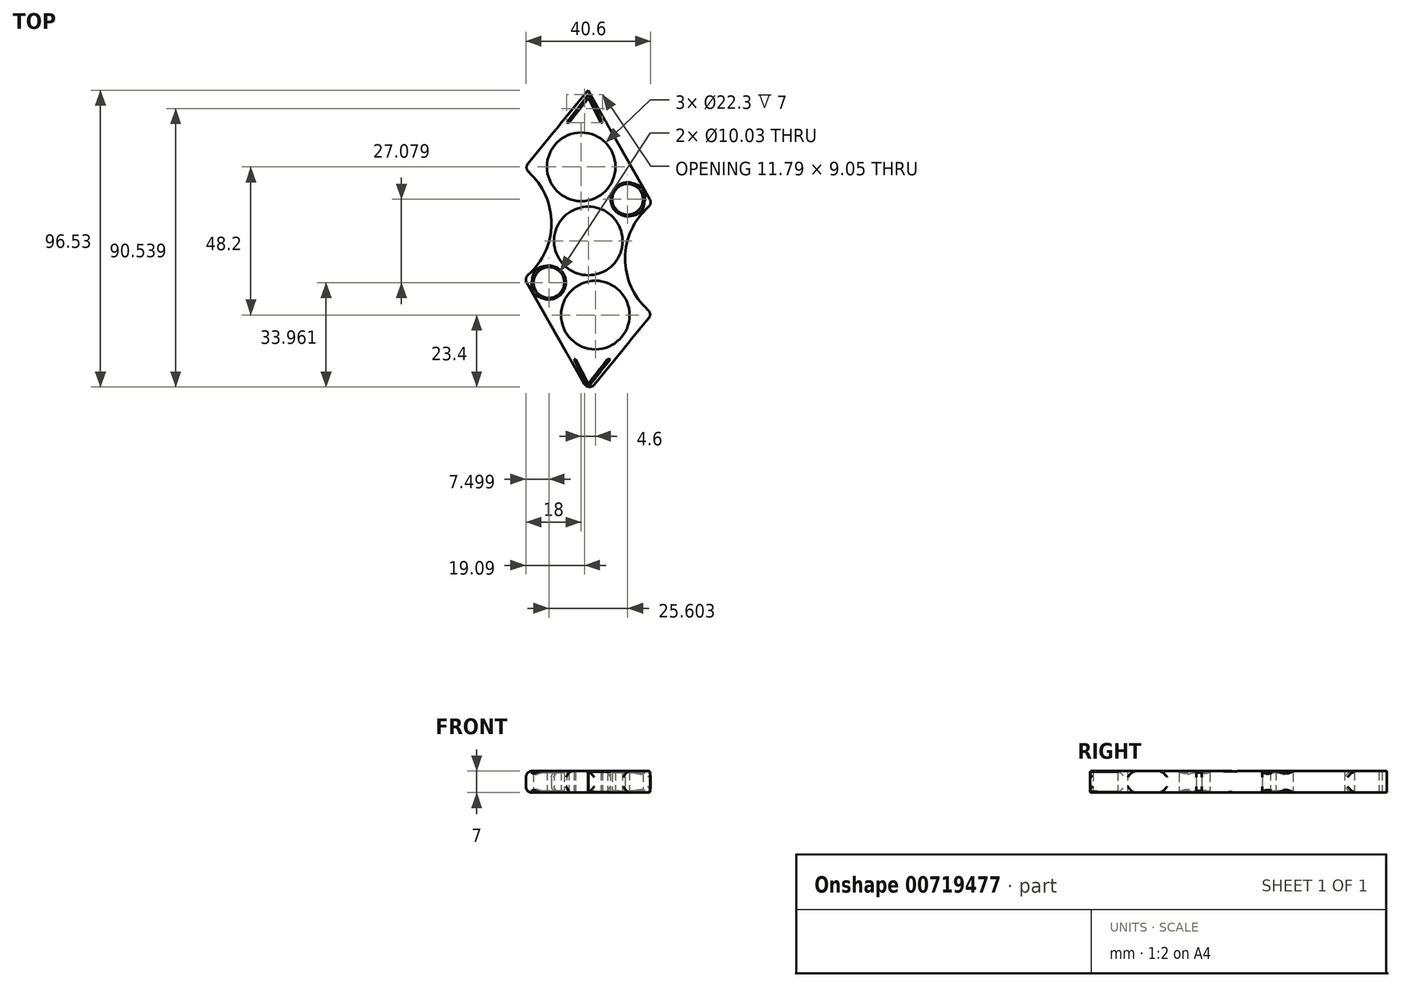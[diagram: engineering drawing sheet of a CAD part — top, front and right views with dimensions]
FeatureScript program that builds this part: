
annotation { "Feature Type Name" : "Feature", "Feature Type Description" : "" }
export const myFeature = defineFeature(function(context is Context, id is Id, definition is map)
    precondition{}
    {
        {
            var Q0;
            Q0=qCreatedBy(makeId("Top.planeOp"),FACE);
            var sketch = newSketch(context, id + "F0", { "sketchPlane" : qUnion([Q0])});
            skCircle(sketch, "E0", {"center": v(0, 0) * mm, "radius": 11.15 * mm});
            skCircle(sketch, "E1", {"center": v(0, 0) * mm, "radius": 12.15 * mm});
            skPoint(sketch, "E2", {"position": v(0, 12.15) * mm});
            skPoint(sketch, "E3", {"position": v(0, -12.15) * mm});
            skPoint(sketch, "E4", {"position": v(-20.9, 23.65) * mm});
            skLineSegment(sketch, "E5", {"start": v(-20.9, 23.65) * mm, "end": v(-9.47, 37.54) * mm});
            skCircle(sketch, "E6.1.0.0", {"center": v(-2.3, 24.1) * mm, "radius": 11.15 * mm});
            skCircle(sketch, "E6.1.0.1", {"center": v(-2.3, 24.1) * mm, "radius": 12.15 * mm});
            skLineSegment(sketch, "E6.direction1", {"start": v(0, 0) * mm, "end": v(-2.3, 24.1) * mm, "construction": true});
            skPoint(sketch, "E7.orphan", {"position": v(-11.2, 12.15) * mm});
            skLineSegment(sketch, "E8.1.0", {"start": v(20.9, -23.65) * mm, "end": v(11.35, -35.25) * mm});
            skLineSegment(sketch, "E8.1.1", {"start": v(-7.16, -36.23) * mm, "end": v(-20.88, -12.14) * mm});
            skPoint(sketch, "E9.orphan", {"position": v(10.73, -12.15) * mm});
            skCircle(sketch, "E10.1.0", {"center": v(2.3, -24.1) * mm, "radius": 11.15 * mm});
            skCircle(sketch, "E10.1.1", {"center": v(2.3, -24.1) * mm, "radius": 12.15 * mm});
            skCircle(sketch, "E11", {"center": v(12.8, 13.54) * mm, "radius": 5.01 * mm});
            skCircle(sketch, "E12.1.0", {"center": v(-12.8, -13.54) * mm, "radius": 5.01 * mm});
            skPoint(sketch, "E13.orphan", {"position": v(0, 60.23) * mm});
            skPoint(sketch, "E14.orphan", {"position": v(-16.16, 31.2) * mm});
            skPoint(sketch, "E15.orphan", {"position": v(0, 56.97) * mm});
            skPoint(sketch, "E16.orphan", {"position": v(15.33, 24.1) * mm});
            skPoint(sketch, "E17.orphan", {"position": v(0, -60.23) * mm});
            skPoint(sketch, "E18.orphan", {"position": v(-0.02, -56.98) * mm});
            skPoint(sketch, "E19.orphan", {"position": v(16.16, -31.2) * mm});
            skPoint(sketch, "E20.orphan", {"position": v(0, 49.07) * mm});
            skPoint(sketch, "E21.orphan", {"position": v(0, 51.35) * mm});
            skPoint(sketch, "E22.orphan", {"position": v(0, 53.8) * mm});
            skPoint(sketch, "E23.orphan", {"position": v(0.08, -48.94) * mm});
            skLineSegment(sketch, "E24.1.0", {"start": v(-7.16, -36.23) * mm, "end": v(0.08, -49.03) * mm});
            skLineSegment(sketch, "E24.1.3", {"start": v(11.35, -35.25) * mm, "end": v(0.08, -49.03) * mm});
            skPoint(sketch, "E25.orphan", {"position": v(11.27, -37.54) * mm});
            skPoint(sketch, "E26.orphan", {"position": v(10.41, -37.54) * mm});
            skPoint(sketch, "E27.orphan", {"position": v(-11.27, 37.54) * mm});
            skPoint(sketch, "E28.orphan", {"position": v(-10.41, 37.54) * mm});
            skPoint(sketch, "E29.center", {"position": v(0.04, 0.02) * mm});
            skPoint(sketch, "E30.start.orphan", {"position": v(20.88, 12.15) * mm});
            skPoint(sketch, "E31.orphan", {"position": v(20.88, 12.14) * mm});
            skPoint(sketch, "E32.orphan", {"position": v(20.96, 12.7) * mm});
            skPoint(sketch, "E33.orphan", {"position": v(-20.66, -12.66) * mm});
            skPoint(sketch, "E34.start.orphan", {"position": v(-20.88, -12.14) * mm});
            skLineSegment(sketch, "E35", {"start": v(-20.9, -12.15) * mm, "end": v(-20.9, -12.15) * mm});
            skArc(sketch, "E36", {"start": v(-20.88, -12.14) * mm, "mid": v(-11.98, 5.76) * mm, "end": v(-20.9, 23.65) * mm});
            skPoint(sketch, "E37.orphan", {"position": v(-8.87, -37.46) * mm});
            skPoint(sketch, "E38.orphan", {"position": v(-7.98, -37.46) * mm});
            skPoint(sketch, "E39.start.orphan", {"position": v(-20.88, -12.66) * mm});
            skLineSegment(sketch, "E40.1.0", {"start": v(7.16, 36.23) * mm, "end": v(20.88, 12.14) * mm});
            skLineSegment(sketch, "E40.1.1", {"start": v(7.16, 36.23) * mm, "end": v(-0.08, 49.03) * mm});
            skLineSegment(sketch, "E40.1.2", {"start": v(-11.35, 35.25) * mm, "end": v(-0.08, 49.03) * mm});
            skLineSegment(sketch, "E40.1.3", {"start": v(-20.9, 23.65) * mm, "end": v(-11.35, 35.25) * mm});
            skArc(sketch, "E40.1.5", {"start": v(20.88, 12.14) * mm, "mid": v(11.98, -5.76) * mm, "end": v(20.9, -23.65) * mm});
            skPoint(sketch, "E41.middle", {"position": v(-1.24, 37.73) * mm});
            skPoint(sketch, "E42.middle", {"position": v(-1.2, 39.16) * mm});
            skLineSegment(sketch, "E43.bottom", {"start": v(4.69, 38.51) * mm, "end": v(-7.1, 38.51) * mm});
            skLineSegment(sketch, "E43.top", {"start": v(4.69, 37.5) * mm, "end": v(-7.1, 37.5) * mm});
            skLineSegment(sketch, "E43.left", {"start": v(4.69, 38.51) * mm, "end": v(4.69, 37.5) * mm});
            skLineSegment(sketch, "E43.right", {"start": v(-7.1, 38.51) * mm, "end": v(-7.1, 37.5) * mm});
            skPoint(sketch, "E43.middle", {"position": v(-1.2, 38.01) * mm});
            skLineSegment(sketch, "E44", {"start": v(-7.1, 38.51) * mm, "end": v(0, 47.56) * mm});
            skLineSegment(sketch, "E45", {"start": v(0, 47.56) * mm, "end": v(4.69, 38.51) * mm});
            skLineSegment(sketch, "E46", {"start": v(-6.23, 38.51) * mm, "end": v(0, 46.45) * mm});
            skLineSegment(sketch, "E47", {"start": v(0, 46.45) * mm, "end": v(4.1, 38.51) * mm});
            skLineSegment(sketch, "E48.1.0", {"start": v(7.1, -38.51) * mm, "end": v(0, -47.56) * mm});
            skLineSegment(sketch, "E48.1.1", {"start": v(6.23, -38.51) * mm, "end": v(0, -46.45) * mm});
            skLineSegment(sketch, "E48.1.2", {"start": v(0, -46.45) * mm, "end": v(-4.1, -38.51) * mm});
            skLineSegment(sketch, "E48.1.3", {"start": v(0, -47.56) * mm, "end": v(-4.69, -38.51) * mm});
            skLineSegment(sketch, "E48.1.4", {"start": v(-4.69, -38.51) * mm, "end": v(7.1, -38.51) * mm});
            skLineSegment(sketch, "E48.1.5", {"start": v(-4.69, -37.5) * mm, "end": v(7.1, -37.5) * mm});
            skLineSegment(sketch, "E48.1.6", {"start": v(7.1, -38.51) * mm, "end": v(7.1, -37.5) * mm});
            skLineSegment(sketch, "E48.1.7", {"start": v(-4.69, -38.51) * mm, "end": v(-4.69, -37.5) * mm});
            skSolve(sketch);
        }
        {
            var Q0;
            Q0=makeQuery(id+"F0.imprint","IMPRINT",FACE,{"disambiguationData":[TD([[makeQuery(id+"F0.imprint","IMPRINT",EDGE,{"derivedFrom":sQuery(id+"F0.wireOp",EDGE,"E11")}),-1.0]])]});
            var Q1;
            {var subQ0=sQuery(id+"F0.wireOp",EDGE,"E6.1.0.1");var subQ1=sQuery(id+"F0.wireOp",EDGE,"E1");var subQ2=makeQuery(id+"F0.imprint","INTERSECT",VERTEX,{"disambiguationData":[OD(0.0)],"derivedFrom":[subQ1,subQ0]});Q1=makeQuery(id+"F0.imprint","IMPRINT",FACE,{"disambiguationData":[TD([[makeQuery(id+"F0.imprint","IMPRINT",EDGE,{"disambiguationData":[TD([[subQ2,1.0]])],"derivedFrom":subQ1}),1.0]])]});}
            var Q2;
            Q2=makeQuery(id+"F0.imprint","IMPRINT",FACE,{"disambiguationData":[TD([[makeQuery(id+"F0.imprint","IMPRINT",EDGE,{"derivedFrom":sQuery(id+"F0.wireOp",EDGE,"E6.1.0.0")}),-1.0]])]});
            var Q3;
            Q3=makeQuery(id+"F0.imprint","IMPRINT",FACE,{"disambiguationData":[TD([[makeQuery(id+"F0.imprint","IMPRINT",EDGE,{"derivedFrom":sQuery(id+"F0.wireOp",EDGE,"E0")}),-1.0]])]});
            var Q4;
            {var subQ0=sQuery(id+"F0.wireOp",EDGE,"E10.1.1");var subQ1=sQuery(id+"F0.wireOp",EDGE,"E1");var subQ2=makeQuery(id+"F0.imprint","INTERSECT",VERTEX,{"disambiguationData":[OD(0.0)],"derivedFrom":[subQ1,subQ0]});Q4=makeQuery(id+"F0.imprint","IMPRINT",FACE,{"disambiguationData":[TD([[makeQuery(id+"F0.imprint","IMPRINT",EDGE,{"disambiguationData":[TD([[subQ2,-1.0]])],"derivedFrom":subQ1}),1.0]])]});}
            var Q5;
            Q5=makeQuery(id+"F0.imprint","IMPRINT",FACE,{"disambiguationData":[TD([[makeQuery(id+"F0.imprint","IMPRINT",EDGE,{"derivedFrom":sQuery(id+"F0.wireOp",EDGE,"E10.1.0")}),-1.0]])]});
            var Q6;
            {var subQ3=sQuery(id+"F0.wireOp",EDGE,"404e12de-fc07-431e-bb74-34cef7439358.1.2");Q6=makeQuery(id+"F0.imprint","IMPRINT",FACE,{"disambiguationData":[TD([[makeQuery(id+"F0.imprint","IMPRINT",EDGE,{"derivedFrom":subQ3}),1.0]])]});}
            var Q7;
            {var subQ1=sQuery(id+"F0.wireOp",EDGE,"h6pCaqxy-B8wU-rt14-AIcK-k2s9Z7jrGcMR");var subQ3=sQuery(id+"F0.wireOp",EDGE,"lE6YIN8j-MXmh-GFKI-PY91-Y5lloAArSDez");var subQ4=makeQuery(id+"F0.imprint","INTERSECT",VERTEX,{"derivedFrom":[subQ1,subQ3]});Q7=makeQuery(id+"F0.imprint","IMPRINT",FACE,{"disambiguationData":[TD([[makeQuery(id+"F0.imprint","IMPRINT",EDGE,{"disambiguationData":[TD([[subQ4,1.0]])],"derivedFrom":subQ3}),-1.0]])]});}
            var Q8;
            {var subQ1=sQuery(id+"F0.wireOp",EDGE,"tINCZcyB-mVGi-bMKS-f95S-jX75Qnie2RH6");var subQ3=sQuery(id+"F0.wireOp",EDGE,"lE6YIN8j-MXmh-GFKI-PY91-Y5lloAArSDez");var subQ4=makeQuery(id+"F0.imprint","INTERSECT",VERTEX,{"derivedFrom":[subQ1,subQ3]});Q8=makeQuery(id+"F0.imprint","IMPRINT",FACE,{"disambiguationData":[TD([[makeQuery(id+"F0.imprint","IMPRINT",EDGE,{"disambiguationData":[TD([[subQ4,1.0]])],"derivedFrom":subQ3}),-1.0]])]});}
            var Q9;
            {var subQ1=sQuery(id+"F0.wireOp",EDGE,"E5");var subQ3=sQuery(id+"F0.wireOp",EDGE,"lE6YIN8j-MXmh-GFKI-PY91-Y5lloAArSDez");var subQ4=makeQuery(id+"F0.imprint","INTERSECT",VERTEX,{"derivedFrom":[subQ1,subQ3]});Q9=makeQuery(id+"F0.imprint","IMPRINT",FACE,{"disambiguationData":[TD([[makeQuery(id+"F0.imprint","IMPRINT",EDGE,{"disambiguationData":[TD([[subQ4,1.0]])],"derivedFrom":subQ3}),-1.0]])]});}
            var Q10;
            {var subQ0=sQuery(id+"F0.wireOp",EDGE,"39fNsugu-ALfK-LRl9-nKP0-bhiYvK7YF85c");var subQ1=sQuery(id+"F0.wireOp",EDGE,"BFZJoNj1-uLuH-64HP-xyf1-DP8Vecsypfw4");var subQ2=makeQuery(id+"F0.imprint","INTERSECT",VERTEX,{"derivedFrom":[subQ1,subQ0]});Q10=makeQuery(id+"F0.imprint","IMPRINT",FACE,{"disambiguationData":[TD([[makeQuery(id+"F0.imprint","IMPRINT",EDGE,{"disambiguationData":[TD([[subQ2,-1.0]])],"derivedFrom":subQ1}),1.0]])]});}
            var Q11;
            {var subQ0=sQuery(id+"F0.wireOp",EDGE,"39fNsugu-ALfK-LRl9-nKP0-bhiYvK7YF85c");var subQ1=sQuery(id+"F0.wireOp",EDGE,"tyitabaC-93li-9vWq-NUVs-itCcroujUFUU");var subQ2=makeQuery(id+"F0.imprint","INTERSECT",VERTEX,{"derivedFrom":[subQ1,subQ0]});Q11=makeQuery(id+"F0.imprint","IMPRINT",FACE,{"disambiguationData":[TD([[makeQuery(id+"F0.imprint","IMPRINT",EDGE,{"disambiguationData":[TD([[subQ2,-1.0]])],"derivedFrom":subQ1}),1.0]])]});}
            var Q12;
            {var subQ0=sQuery(id+"F0.wireOp",EDGE,"39fNsugu-ALfK-LRl9-nKP0-bhiYvK7YF85c");var subQ1=sQuery(id+"F0.wireOp",EDGE,"ImIDgHrk-oYtM-6ggm-x5GL-kRbq2VFvojzK");var subQ2=makeQuery(id+"F0.imprint","INTERSECT",VERTEX,{"derivedFrom":[subQ1,subQ0]});Q12=makeQuery(id+"F0.imprint","IMPRINT",FACE,{"disambiguationData":[TD([[makeQuery(id+"F0.imprint","IMPRINT",EDGE,{"disambiguationData":[TD([[subQ2,-1.0]])],"derivedFrom":subQ1}),1.0]])]});}
            var Q13;
            {var subQ0=sQuery(id+"F0.wireOp",EDGE,"404e12de-fc07-431e-bb74-34cef7439358.1.1");Q13=makeQuery(id+"F0.imprint","IMPRINT",FACE,{"disambiguationData":[TD([[makeQuery(id+"F0.imprint","IMPRINT",EDGE,{"derivedFrom":subQ0}),-1.0]])]});}
            var Q14;
            {var subQ1=sQuery(id+"F0.wireOp",EDGE,"E8.1.0");var subQ3=sQuery(id+"F0.wireOp",EDGE,"870a5f02-87da-4261-8491-2a3d2da184ff.1.1");var subQ4=makeQuery(id+"F0.imprint","INTERSECT",VERTEX,{"derivedFrom":[subQ1,subQ3]});Q14=makeQuery(id+"F0.imprint","IMPRINT",FACE,{"disambiguationData":[TD([[makeQuery(id+"F0.imprint","IMPRINT",EDGE,{"disambiguationData":[TD([[subQ4,1.0]])],"derivedFrom":subQ3}),-1.0]])]});}
            var Q15;
            {var subQ1=sQuery(id+"F0.wireOp",EDGE,"dd0263d1-3455-4b8a-9925-82208476033f.1.2");var subQ3=sQuery(id+"F0.wireOp",EDGE,"870a5f02-87da-4261-8491-2a3d2da184ff.1.1");var subQ4=makeQuery(id+"F0.imprint","INTERSECT",VERTEX,{"derivedFrom":[subQ1,subQ3]});Q15=makeQuery(id+"F0.imprint","IMPRINT",FACE,{"disambiguationData":[TD([[makeQuery(id+"F0.imprint","IMPRINT",EDGE,{"disambiguationData":[TD([[subQ4,-1.0]])],"derivedFrom":subQ3}),-1.0]])]});}
            var Q16;
            {var subQ0=sQuery(id+"F0.wireOp",EDGE,"dd0263d1-3455-4b8a-9925-82208476033f.1.2");var subQ3=sQuery(id+"F0.wireOp",EDGE,"870a5f02-87da-4261-8491-2a3d2da184ff.1.1");var subQ5=makeQuery(id+"F0.imprint","INTERSECT",VERTEX,{"derivedFrom":[subQ0,subQ3]});Q16=makeQuery(id+"F0.imprint","IMPRINT",FACE,{"disambiguationData":[TD([[makeQuery(id+"F0.imprint","IMPRINT",EDGE,{"disambiguationData":[TD([[subQ5,1.0]])],"derivedFrom":subQ3}),-1.0]])]});}
            var Q17;
            {var subQ3=sQuery(id+"F0.wireOp",EDGE,"njGUlkdr-dbbk-PcjP-8qjy-DrNTBEdDoYfP");Q17=makeQuery(id+"F0.imprint","IMPRINT",FACE,{"disambiguationData":[TD([[makeQuery(id+"F0.imprint","IMPRINT",EDGE,{"derivedFrom":subQ3}),1.0]])]});}
            var Q18;
            {var subQ0=sQuery(id+"F0.wireOp",EDGE,"LZuvuBFe-pqvT-4oDd-noRx-V0Hc8yvodrcx");Q18=makeQuery(id+"F0.imprint","IMPRINT",FACE,{"disambiguationData":[TD([[makeQuery(id+"F0.imprint","IMPRINT",EDGE,{"derivedFrom":subQ0}),-1.0]])]});}
            var Q19;
            {var subQ0=sQuery(id+"F0.wireOp",EDGE,"870a5f02-87da-4261-8491-2a3d2da184ff.1.0");var subQ1=sQuery(id+"F0.wireOp",EDGE,"dd0263d1-3455-4b8a-9925-82208476033f.1.5");var subQ2=makeQuery(id+"F0.imprint","INTERSECT",VERTEX,{"derivedFrom":[subQ1,subQ0]});Q19=makeQuery(id+"F0.imprint","IMPRINT",FACE,{"disambiguationData":[TD([[makeQuery(id+"F0.imprint","IMPRINT",EDGE,{"disambiguationData":[TD([[subQ2,-1.0]])],"derivedFrom":subQ1}),1.0]])]});}
            var Q20;
            {var subQ0=sQuery(id+"F0.wireOp",EDGE,"870a5f02-87da-4261-8491-2a3d2da184ff.1.0");var subQ1=sQuery(id+"F0.wireOp",EDGE,"dd0263d1-3455-4b8a-9925-82208476033f.1.4");var subQ2=makeQuery(id+"F0.imprint","INTERSECT",VERTEX,{"derivedFrom":[subQ1,subQ0]});Q20=makeQuery(id+"F0.imprint","IMPRINT",FACE,{"disambiguationData":[TD([[makeQuery(id+"F0.imprint","IMPRINT",EDGE,{"disambiguationData":[TD([[subQ2,-1.0]])],"derivedFrom":subQ1}),1.0]])]});}
            var Q21;
            {var subQ0=sQuery(id+"F0.wireOp",EDGE,"870a5f02-87da-4261-8491-2a3d2da184ff.1.0");var subQ1=sQuery(id+"F0.wireOp",EDGE,"E8.1.1");var subQ2=makeQuery(id+"F0.imprint","INTERSECT",VERTEX,{"derivedFrom":[subQ1,subQ0]});Q21=makeQuery(id+"F0.imprint","IMPRINT",FACE,{"disambiguationData":[TD([[makeQuery(id+"F0.imprint","IMPRINT",EDGE,{"disambiguationData":[TD([[subQ2,-1.0]])],"derivedFrom":subQ1}),1.0]])]});}
            var Q22;
            {var subQ0=sQuery(id+"F0.wireOp",EDGE,"dd0263d1-3455-4b8a-9925-82208476033f.1.5");var subQ1=sQuery(id+"F0.wireOp",EDGE,"dd0263d1-3455-4b8a-9925-82208476033f.1.2");var subQ2=makeQuery(id+"F0.imprint","INTERSECT",VERTEX,{"derivedFrom":[subQ1,subQ0]});Q22=makeQuery(id+"F0.imprint","IMPRINT",FACE,{"disambiguationData":[TD([[makeQuery(id+"F0.imprint","IMPRINT",EDGE,{"disambiguationData":[TD([[subQ2,1.0]])],"derivedFrom":subQ1}),-1.0]])]});}
            var Q23;
            {var subQ4=sQuery(id+"F0.wireOp",EDGE,"njGUlkdr-dbbk-PcjP-8qjy-DrNTBEdDoYfP");Q23=makeQuery(id+"F0.imprint","IMPRINT",FACE,{"disambiguationData":[TD([[makeQuery(id+"F0.imprint","IMPRINT",EDGE,{"derivedFrom":subQ4}),-1.0]])]});}
            var Q24;
            {var subQ0=sQuery(id+"F0.wireOp",EDGE,"404e12de-fc07-431e-bb74-34cef7439358.1.1");Q24=makeQuery(id+"F0.imprint","IMPRINT",FACE,{"disambiguationData":[TD([[makeQuery(id+"F0.imprint","IMPRINT",EDGE,{"derivedFrom":subQ0}),1.0]])]});}
            var Q25;
            {var subQ5=sQuery(id+"F0.wireOp",EDGE,"tyitabaC-93li-9vWq-NUVs-itCcroujUFUU");var subQ6=sQuery(id+"F0.wireOp",EDGE,"tINCZcyB-mVGi-bMKS-f95S-jX75Qnie2RH6");var subQ7=makeQuery(id+"F0.imprint","INTERSECT",VERTEX,{"derivedFrom":[subQ6,subQ5]});Q25=makeQuery(id+"F0.imprint","IMPRINT",FACE,{"disambiguationData":[TD([[makeQuery(id+"F0.imprint","IMPRINT",EDGE,{"disambiguationData":[TD([[subQ7,1.0]])],"derivedFrom":subQ6}),1.0]])]});}
            var Q26;
            {var subQ3=sQuery(id+"F0.wireOp",EDGE,"39fNsugu-ALfK-LRl9-nKP0-bhiYvK7YF85c");var subQ5=sQuery(id+"F0.wireOp",EDGE,"ImIDgHrk-oYtM-6ggm-x5GL-kRbq2VFvojzK");var subQ7=makeQuery(id+"F0.imprint","INTERSECT",VERTEX,{"derivedFrom":[subQ5,subQ3]});Q26=makeQuery(id+"F0.imprint","IMPRINT",FACE,{"disambiguationData":[TD([[makeQuery(id+"F0.imprint","IMPRINT",EDGE,{"disambiguationData":[TD([[subQ7,1.0]])],"derivedFrom":subQ3}),1.0]])]});}
            var Q27;
            {var subQ3=sQuery(id+"F0.wireOp",EDGE,"PDSIkljy-w7Nh-ABX0-YaZa-quTeSK1Cx2aV");var subQ5=sQuery(id+"F0.wireOp",EDGE,"IVrAgTxp-ZFo3-gWKH-pwNR-pWNfuUDz9w63");var subQ6=makeQuery(id+"F0.imprint","INTERSECT",VERTEX,{"derivedFrom":[subQ3,subQ5]});Q27=makeQuery(id+"F0.imprint","IMPRINT",FACE,{"disambiguationData":[TD([[makeQuery(id+"F0.imprint","IMPRINT",EDGE,{"disambiguationData":[TD([[subQ6,-1.0]])],"derivedFrom":subQ5}),1.0]])]});}
            var Q28;
            {var subQ1=sQuery(id+"F0.wireOp",EDGE,"eSBNZSpG-FLNo-ULSt-k6ad-Sugn7jTvAHCc");var subQ3=makeQuery(id+"F0.imprint","INTERSECT",VERTEX,{"derivedFrom":[subQ1,sQuery(id+"F0.wireOp",EDGE,"IVrAgTxp-ZFo3-gWKH-pwNR-pWNfuUDz9w63")]});Q28=makeQuery(id+"F0.imprint","IMPRINT",FACE,{"disambiguationData":[TD([[makeQuery(id+"F0.imprint","IMPRINT",EDGE,{"disambiguationData":[TD([[subQ3,1.0]])],"derivedFrom":subQ1}),1.0]])]});}
            var Q29;
            {var subQ0=sQuery(id+"F0.wireOp",EDGE,"PDSIkljy-w7Nh-ABX0-YaZa-quTeSK1Cx2aV");var subQ3=sQuery(id+"F0.wireOp",EDGE,"IVrAgTxp-ZFo3-gWKH-pwNR-pWNfuUDz9w63");var subQ5=makeQuery(id+"F0.imprint","INTERSECT",VERTEX,{"derivedFrom":[subQ0,subQ3]});Q29=makeQuery(id+"F0.imprint","IMPRINT",FACE,{"disambiguationData":[TD([[makeQuery(id+"F0.imprint","IMPRINT",EDGE,{"disambiguationData":[TD([[subQ5,-1.0]])],"derivedFrom":subQ3}),-1.0]])]});}
            var Q30;
            {var subQ1=sQuery(id+"F0.wireOp",EDGE,"eSBNZSpG-FLNo-ULSt-k6ad-Sugn7jTvAHCc");var subQ3=sQuery(id+"F0.wireOp",EDGE,"IVrAgTxp-ZFo3-gWKH-pwNR-pWNfuUDz9w63");var subQ4=makeQuery(id+"F0.imprint","INTERSECT",VERTEX,{"derivedFrom":[subQ1,subQ3]});Q30=makeQuery(id+"F0.imprint","IMPRINT",FACE,{"disambiguationData":[TD([[makeQuery(id+"F0.imprint","IMPRINT",EDGE,{"disambiguationData":[TD([[subQ4,1.0]])],"derivedFrom":subQ3}),-1.0]])]});}
            var Q31;
            {var subQ1=sQuery(id+"F0.wireOp",EDGE,"4nxL0UMP-Uj5N-17f7-JIDu-PR7GllYYYLHz");var subQ3=sQuery(id+"F0.wireOp",EDGE,"bdf63c88-88f9-45a5-954a-d38f824fd993.trimOffspring");var subQ4=makeQuery(id+"F0.imprint","INTERSECT",VERTEX,{"derivedFrom":[subQ1,subQ3]});Q31=makeQuery(id+"F0.imprint","IMPRINT",FACE,{"disambiguationData":[TD([[makeQuery(id+"F0.imprint","IMPRINT",EDGE,{"disambiguationData":[TD([[subQ4,-1.0]])],"derivedFrom":subQ3}),-1.0]])]});}
            var Q32;
            {var subQ0=sQuery(id+"F0.wireOp",EDGE,"lVHEMNya-pRbu-zRd5-eP6L-49l2YV8NTstR");var subQ3=sQuery(id+"F0.wireOp",EDGE,"bdf63c88-88f9-45a5-954a-d38f824fd993.trimOffspring");var subQ5=makeQuery(id+"F0.imprint","INTERSECT",VERTEX,{"derivedFrom":[subQ0,subQ3]});Q32=makeQuery(id+"F0.imprint","IMPRINT",FACE,{"disambiguationData":[TD([[makeQuery(id+"F0.imprint","IMPRINT",EDGE,{"disambiguationData":[TD([[subQ5,1.0]])],"derivedFrom":subQ3}),-1.0]])]});}
            var Q33;
            {var subQ3=sQuery(id+"F0.wireOp",EDGE,"lVHEMNya-pRbu-zRd5-eP6L-49l2YV8NTstR");var subQ5=sQuery(id+"F0.wireOp",EDGE,"bdf63c88-88f9-45a5-954a-d38f824fd993.trimOffspring");var subQ7=makeQuery(id+"F0.imprint","INTERSECT",VERTEX,{"derivedFrom":[subQ3,subQ5]});Q33=makeQuery(id+"F0.imprint","IMPRINT",FACE,{"disambiguationData":[TD([[makeQuery(id+"F0.imprint","IMPRINT",EDGE,{"disambiguationData":[TD([[subQ7,1.0]])],"derivedFrom":subQ5}),1.0]])]});}
            var Q34;
            {var subQ3=sQuery(id+"F0.wireOp",EDGE,"lE6YIN8j-MXmh-GFKI-PY91-Y5lloAArSDez");var subQ5=sQuery(id+"F0.wireOp",EDGE,"h6pCaqxy-B8wU-rt14-AIcK-k2s9Z7jrGcMR");var subQ7=makeQuery(id+"F0.imprint","INTERSECT",VERTEX,{"derivedFrom":[subQ5,subQ3]});Q34=makeQuery(id+"F0.imprint","IMPRINT",FACE,{"disambiguationData":[TD([[makeQuery(id+"F0.imprint","IMPRINT",EDGE,{"disambiguationData":[TD([[subQ7,-1.0]])],"derivedFrom":subQ3}),1.0]])]});}
            var Q35;
            {var subQ4=sQuery(id+"F0.wireOp",EDGE,"E24.1.0");var subQ6=makeQuery(id+"F0.imprint","INTERSECT",VERTEX,{"derivedFrom":[subQ4,sQuery(id+"F0.wireOp",EDGE,"b9749ddf-a8bf-4797-920b-2e4a02c3e957.1.0")]});Q35=makeQuery(id+"F0.imprint","IMPRINT",FACE,{"disambiguationData":[TD([[makeQuery(id+"F0.imprint","IMPRINT",EDGE,{"disambiguationData":[TD([[subQ6,1.0]])],"derivedFrom":subQ4}),1.0]])]});}
            var Q36;
            {var subQ1=sQuery(id+"F0.wireOp",EDGE,"dd0263d1-3455-4b8a-9925-82208476033f.1.2");var subQ3=sQuery(id+"F0.wireOp",EDGE,"870a5f02-87da-4261-8491-2a3d2da184ff.1.1");var subQ4=makeQuery(id+"F0.imprint","INTERSECT",VERTEX,{"derivedFrom":[subQ1,subQ3]});Q36=makeQuery(id+"F0.imprint","IMPRINT",FACE,{"disambiguationData":[TD([[makeQuery(id+"F0.imprint","IMPRINT",EDGE,{"disambiguationData":[TD([[subQ4,-1.0]])],"derivedFrom":subQ3}),1.0]])]});}
            var Q37;
            {var subQ0=sQuery(id+"F0.wireOp",EDGE,"E24.1.5");var subQ5=sQuery(id+"F0.wireOp",EDGE,"b9749ddf-a8bf-4797-920b-2e4a02c3e957.1.1");var subQ7=makeQuery(id+"F0.imprint","INTERSECT",VERTEX,{"derivedFrom":[subQ0,subQ5]});Q37=makeQuery(id+"F0.imprint","IMPRINT",FACE,{"disambiguationData":[TD([[makeQuery(id+"F0.imprint","IMPRINT",EDGE,{"disambiguationData":[TD([[subQ7,1.0]])],"derivedFrom":subQ5}),1.0]])]});}
            var Q38;
            {var subQ3=sQuery(id+"F0.wireOp",EDGE,"E24.1.2");var subQ5=sQuery(id+"F0.wireOp",EDGE,"b9749ddf-a8bf-4797-920b-2e4a02c3e957.1.0");var subQ7=makeQuery(id+"F0.imprint","INTERSECT",VERTEX,{"derivedFrom":[subQ3,subQ5]});Q38=makeQuery(id+"F0.imprint","IMPRINT",FACE,{"disambiguationData":[TD([[makeQuery(id+"F0.imprint","IMPRINT",EDGE,{"disambiguationData":[TD([[subQ7,-1.0]])],"derivedFrom":subQ5}),1.0]])]});}
            var Q39;
            {var subQ3=sQuery(id+"F0.wireOp",EDGE,"870a5f02-87da-4261-8491-2a3d2da184ff.1.0");var subQ5=sQuery(id+"F0.wireOp",EDGE,"dd0263d1-3455-4b8a-9925-82208476033f.1.5");var subQ6=makeQuery(id+"F0.imprint","INTERSECT",VERTEX,{"derivedFrom":[subQ5,subQ3]});Q39=makeQuery(id+"F0.imprint","IMPRINT",FACE,{"disambiguationData":[TD([[makeQuery(id+"F0.imprint","IMPRINT",EDGE,{"disambiguationData":[TD([[subQ6,1.0]])],"derivedFrom":subQ3}),1.0]])]});}
            var Q40;
            {var subQ0=sQuery(id+"F0.wireOp",EDGE,"E24.1.5");var subQ3=sQuery(id+"F0.wireOp",EDGE,"b9749ddf-a8bf-4797-920b-2e4a02c3e957.1.1");var subQ5=makeQuery(id+"F0.imprint","INTERSECT",VERTEX,{"derivedFrom":[subQ0,subQ3]});Q40=makeQuery(id+"F0.imprint","IMPRINT",FACE,{"disambiguationData":[TD([[makeQuery(id+"F0.imprint","IMPRINT",EDGE,{"disambiguationData":[TD([[subQ5,1.0]])],"derivedFrom":subQ3}),-1.0]])]});}
            var Q41;
            {var subQ1=sQuery(id+"F0.wireOp",EDGE,"E24.1.3");var subQ3=sQuery(id+"F0.wireOp",EDGE,"b9749ddf-a8bf-4797-920b-2e4a02c3e957.1.1");var subQ4=makeQuery(id+"F0.imprint","INTERSECT",VERTEX,{"derivedFrom":[subQ1,subQ3]});Q41=makeQuery(id+"F0.imprint","IMPRINT",FACE,{"disambiguationData":[TD([[makeQuery(id+"F0.imprint","IMPRINT",EDGE,{"disambiguationData":[TD([[subQ4,-1.0]])],"derivedFrom":subQ3}),-1.0]])]});}
            var Q42;
            {var subQ1=sQuery(id+"F0.wireOp",EDGE,"E24.1.0");var subQ3=sQuery(id+"F0.wireOp",EDGE,"b9749ddf-a8bf-4797-920b-2e4a02c3e957.1.0");var subQ4=makeQuery(id+"F0.imprint","INTERSECT",VERTEX,{"derivedFrom":[subQ1,subQ3]});Q42=makeQuery(id+"F0.imprint","IMPRINT",FACE,{"disambiguationData":[TD([[makeQuery(id+"F0.imprint","IMPRINT",EDGE,{"disambiguationData":[TD([[subQ4,1.0]])],"derivedFrom":subQ3}),-1.0]])]});}
            var Q43;
            {var subQ0=sQuery(id+"F0.wireOp",EDGE,"E24.1.2");var subQ3=sQuery(id+"F0.wireOp",EDGE,"b9749ddf-a8bf-4797-920b-2e4a02c3e957.1.0");var subQ5=makeQuery(id+"F0.imprint","INTERSECT",VERTEX,{"derivedFrom":[subQ0,subQ3]});Q43=makeQuery(id+"F0.imprint","IMPRINT",FACE,{"disambiguationData":[TD([[makeQuery(id+"F0.imprint","IMPRINT",EDGE,{"disambiguationData":[TD([[subQ5,-1.0]])],"derivedFrom":subQ3}),-1.0]])]});}
            var Q44;
            {var subQ0=sQuery(id+"F0.wireOp",EDGE,"IVrAgTxp-ZFo3-gWKH-pwNR-pWNfuUDz9w63");var subQ1=sQuery(id+"F0.wireOp",EDGE,"eSBNZSpG-FLNo-ULSt-k6ad-Sugn7jTvAHCc");var subQ2=makeQuery(id+"F0.imprint","INTERSECT",VERTEX,{"derivedFrom":[subQ1,subQ0]});Q44=makeQuery(id+"F0.imprint","IMPRINT",FACE,{"disambiguationData":[TD([[makeQuery(id+"F0.imprint","IMPRINT",EDGE,{"disambiguationData":[TD([[subQ2,1.0]])],"derivedFrom":subQ1}),-1.0]])]});}
            var Q45;
            {var subQ0=sQuery(id+"F0.wireOp",EDGE,"bdf63c88-88f9-45a5-954a-d38f824fd993.trimOffspring");var subQ1=sQuery(id+"F0.wireOp",EDGE,"4nxL0UMP-Uj5N-17f7-JIDu-PR7GllYYYLHz");var subQ2=makeQuery(id+"F0.imprint","INTERSECT",VERTEX,{"derivedFrom":[subQ1,subQ0]});Q45=makeQuery(id+"F0.imprint","IMPRINT",FACE,{"disambiguationData":[TD([[makeQuery(id+"F0.imprint","IMPRINT",EDGE,{"disambiguationData":[TD([[subQ2,1.0]])],"derivedFrom":subQ1}),1.0]])]});}
            var Q46;
            {var subQ0=sQuery(id+"F0.wireOp",EDGE,"b9749ddf-a8bf-4797-920b-2e4a02c3e957.1.0");var subQ1=sQuery(id+"F0.wireOp",EDGE,"E24.1.0");var subQ2=makeQuery(id+"F0.imprint","INTERSECT",VERTEX,{"derivedFrom":[subQ1,subQ0]});Q46=makeQuery(id+"F0.imprint","IMPRINT",FACE,{"disambiguationData":[TD([[makeQuery(id+"F0.imprint","IMPRINT",EDGE,{"disambiguationData":[TD([[subQ2,1.0]])],"derivedFrom":subQ1}),-1.0]])]});}
            var Q47;
            {var subQ0=sQuery(id+"F0.wireOp",EDGE,"b9749ddf-a8bf-4797-920b-2e4a02c3e957.1.1");var subQ1=sQuery(id+"F0.wireOp",EDGE,"E24.1.3");var subQ2=makeQuery(id+"F0.imprint","INTERSECT",VERTEX,{"derivedFrom":[subQ1,subQ0]});Q47=makeQuery(id+"F0.imprint","IMPRINT",FACE,{"disambiguationData":[TD([[makeQuery(id+"F0.imprint","IMPRINT",EDGE,{"disambiguationData":[TD([[subQ2,1.0]])],"derivedFrom":subQ1}),1.0]])]});}
            var Q48;
            {var subQ3=sQuery(id+"F0.wireOp",EDGE,"coLpdnhY-Vdj6-8FRa-8NRC-qjjY8FqOVJ2b");Q48=makeQuery(id+"F0.imprint","IMPRINT",FACE,{"disambiguationData":[TD([[makeQuery(id+"F0.imprint","IMPRINT",EDGE,{"derivedFrom":subQ3}),-1.0]])]});}
            var Q49;
            {var subQ2=sQuery(id+"F0.wireOp",EDGE,"coLpdnhY-Vdj6-8FRa-8NRC-qjjY8FqOVJ2b");Q49=makeQuery(id+"F0.imprint","IMPRINT",FACE,{"disambiguationData":[TD([[makeQuery(id+"F0.imprint","IMPRINT",EDGE,{"derivedFrom":subQ2}),1.0]])]});}
            var Q50;
            {var subQ4=sQuery(id+"F0.wireOp",EDGE,"E29.1.2");Q50=makeQuery(id+"F0.imprint","IMPRINT",FACE,{"disambiguationData":[TD([[makeQuery(id+"F0.imprint","IMPRINT",EDGE,{"derivedFrom":subQ4}),-1.0]])]});}
            var Q51;
            {var subQ2=sQuery(id+"F0.wireOp",EDGE,"E29.1.2");Q51=makeQuery(id+"F0.imprint","IMPRINT",FACE,{"disambiguationData":[TD([[makeQuery(id+"F0.imprint","IMPRINT",EDGE,{"derivedFrom":subQ2}),1.0]])]});}
            var Q52;
            Q52=makeQuery(id+"F0.imprint","IMPRINT",FACE,{"disambiguationData":[TD([[makeQuery(id+"F0.imprint","IMPRINT",EDGE,{"derivedFrom":sQuery(id+"F0.wireOp",EDGE,"E43.top")}),-1.0]])]});
            var Q53;
            {var subQ0=sQuery(id+"F0.wireOp",EDGE,"E46");Q53=makeQuery(id+"F0.imprint","IMPRINT",FACE,{"disambiguationData":[TD([[makeQuery(id+"F0.imprint","IMPRINT",EDGE,{"derivedFrom":subQ0}),-1.0]])]});}
            var Q54;
            {var subQ0=sQuery(id+"F0.wireOp",EDGE,"E48.1.1");Q54=makeQuery(id+"F0.imprint","IMPRINT",FACE,{"disambiguationData":[TD([[makeQuery(id+"F0.imprint","IMPRINT",EDGE,{"derivedFrom":subQ0}),-1.0]])]});}
            var Q55;
            Q55=makeQuery(id+"F0.imprint","IMPRINT",FACE,{"disambiguationData":[TD([[makeQuery(id+"F0.imprint","IMPRINT",EDGE,{"derivedFrom":sQuery(id+"F0.wireOp",EDGE,"E48.1.5")}),-1.0]])]});
            extrude(context, id + "F1", {"entities" : qUnion([Q0, Q1, Q2, Q3, Q4, Q5, Q6, Q7, Q8, Q9, Q10, Q11, Q12, Q13, Q14, Q15, Q16, Q17, Q18, Q19, Q20, Q21, Q22, Q23, Q24, Q25, Q26, Q27, Q28, Q29, Q30, Q31, Q32, Q33, Q34, Q35, Q36, Q37, Q38, Q39, Q40, Q41, Q42, Q43, Q44, Q45, Q46, Q47, Q48, Q49, Q50, Q51, Q52, Q53, Q54, Q55]), "depth" : 7 * mm, "offsetDistance" : 25 * mm});
        }
        {
            var Q0;
            Q0=makeQuery(id+"F1.opExtrude","SWEPT_FACE",FACE,{"disambiguationData":[OSD([sQuery(id+"F0.wireOp",EDGE,"E40.1.5")])]});
            var Q1;
            Q1=makeQuery(id+"F1.opExtrude","SWEPT_FACE",FACE,{"disambiguationData":[OSD([sQuery(id+"F0.wireOp",EDGE,"E36")])]});
            var Q2;
            Q2=makeQuery(id+"F1.opExtrude","SWEPT_FACE",FACE,{"disambiguationData":[OSD([sQuery(id+"F0.wireOp",EDGE,"E8.1.1")])]});
            var Q3;
            Q3=makeQuery(id+"F1.opExtrude","SWEPT_FACE",FACE,{"disambiguationData":[OSD([sQuery(id+"F0.wireOp",EDGE,"E24.1.3")])]});
            var Q4;
            Q4=makeQuery(id+"F1.opExtrude","SWEPT_FACE",FACE,{"disambiguationData":[OSD([sQuery(id+"F0.wireOp",EDGE,"E40.1.0")])]});
            var Q5;
            Q5=makeQuery(id+"F1.opExtrude","SWEPT_FACE",FACE,{"disambiguationData":[OSD([sQuery(id+"F0.wireOp",EDGE,"E40.1.3")])]});
            fillet(context, id + "F2", {"entities" : qUnion([Q0, Q1, Q2, Q3, Q4, Q5]), "radius" : 2 * mm, "tangentPropagation" : true, "allowEdgeOverflow" : false});
        }
        {
            var Q0;
            Q0=makeQuery(id+"F1.opExtrude","SWEPT_FACE",FACE,{"disambiguationData":[OSD([sQuery(id+"F0.wireOp",EDGE,"E11")])]});
            var Q1;
            Q1=makeQuery(id+"F1.opExtrude","SWEPT_FACE",FACE,{"disambiguationData":[OSD([sQuery(id+"F0.wireOp",EDGE,"E12.1.0")])]});
            chamfer(context, id + "F3", {"entities" : qUnion([Q0, Q1]), "width" : .5 * mm, "tangentPropagation" : true});
        }
    });
